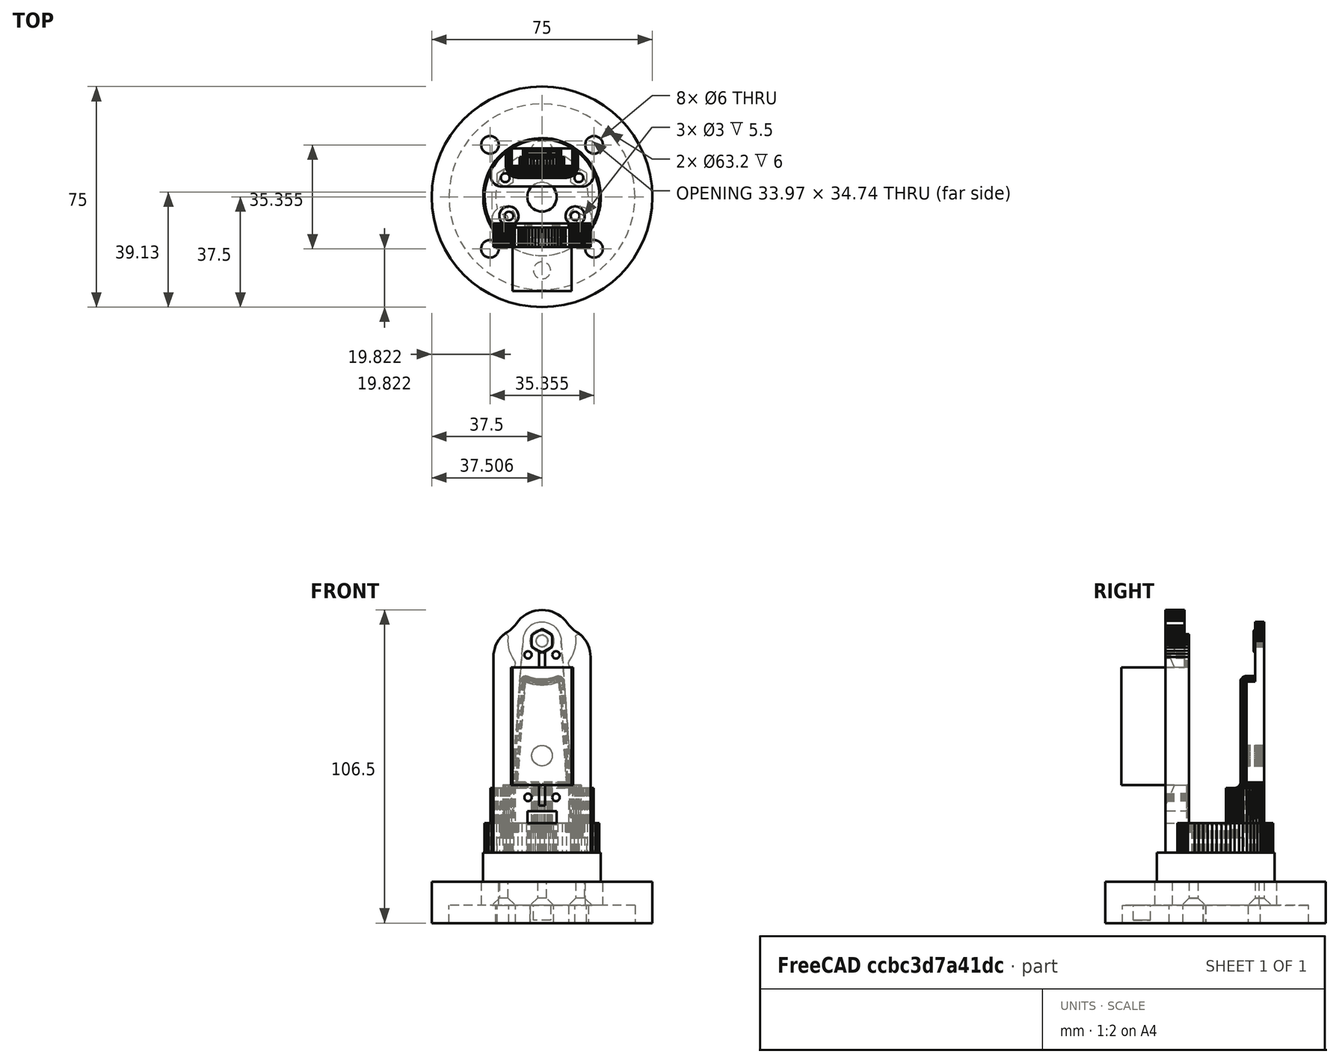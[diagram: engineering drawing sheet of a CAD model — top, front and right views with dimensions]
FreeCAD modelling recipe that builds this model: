
FCSTD DOCUMENT  (FreeCAD 0.16R6703 (Git))
Label: GripperBase
License: All rights reserved
LicenseURL: http://en.wikipedia.org/wiki/All_rights_reserved
objects: Part::Feature×5, Part::MultiFuse×3, Mesh::Feature×2, Sketcher::SketchObject×2, PartDesign::Pad×2
note: 14 computed .brp shape members not serialized (recipe doc carries the construction recipe); baked Part::Feature solids carry a one-line shape summary decoded from their .brp

FEATURE [Mesh::Feature] ServoMount
FEATURE [Mesh::Feature] Mount_B
  Placement = pos=(129.2,99,33.5) rot=(0.707107,-0.707107,0;3.14159rad)
FEATURE [Sketcher::SketchObject] Sketch
  sketch-geometry (4):
    g0: LineSegment StartX=0 StartY=1 StartZ=0 EndX=40 EndY=1 EndZ=0
    g1: LineSegment StartX=40 StartY=1 StartZ=0 EndX=40 EndY=-19 EndZ=0
    g2: LineSegment StartX=40 StartY=-19 StartZ=0 EndX=0 EndY=-19 EndZ=0
    g3: LineSegment StartX=0 StartY=-19 StartZ=0 EndX=0 EndY=1 EndZ=0
  constraints (12):
    c: Coincident(g0,g1)
    c: Coincident(g1,g2)
    c: Coincident(g2,g3)
    c: Horizontal(g0)
    c: Horizontal(g2)
    c: Vertical(g1)
    c: Vertical(g3)
    c: DistanceX(g2,g1) = 40
    c: DistanceY(g1,g0) = 20
    c: Coincident(g3,g0)
    c: PointOnObject(g0,g-2)
    c: DistanceY(g-1,g0) = 1
FEATURE [PartDesign::Pad] Pad
  Length = 15
  Length2 = 100
  Reversed = true
  Sketch = -> Sketch
  Type = 0
FEATURE [Part::Feature] ServoMount001
  shape: bbox 82.5 x 38.99 x 36.48 mm, 2472 faces, 0 solids (baked)
FEATURE [Part::Feature] Mount_B001
  shape: bbox 68.5 x 35.13 x 13 mm, 2276 faces, 0 solids (baked)
FEATURE [Part::Feature] ServoMount001_solid  label="ServoMount001 (Solid)"
  shape: bbox 82.5 x 38.99 x 36.48 mm, 2472 faces (baked)
FEATURE [Part::Feature] Mount_B001_solid  label="Mount_B001 (Solid)"
  shape: bbox 68.5 x 35.13 x 13 mm, 2276 faces (baked)
FEATURE [Part::MultiFuse] Fusion
  Shapes = -> [ServoMount001_solid,Mount_B001_solid]
FEATURE [Part::MultiFuse] Fusion001
  Placement = pos=(10,0,0) rot=(0,0,1;0rad)
  Shapes = -> [Pad,Fusion]
FEATURE [Part::Feature] Pocket001
  Placement = pos=(-31,-9,17) rot=(0.57735,0.57735,0.57735;2.0944rad)
  shape: bbox 14 x 75 x 75 mm, 31 faces (baked)
FEATURE [Part::MultiFuse] Fusion002
  Placement = pos=(9,-17,37) rot=(-0.57735,-0.57735,-0.57735;2.0944rad)
  Shapes = -> [Pocket001,Fusion001]
FEATURE [Sketcher::SketchObject] Sketch001
  Placement = pos=(9,-17,14) rot=(0,0,1;0rad)
  Support = -> Fusion002 [Face33]
  sketch-geometry (1):
    g0: Circle CenterX=-9 CenterY=17 CenterZ=0 NormalX=0 NormalY=0 NormalZ=1 Radius=20
  constraints (3):
    c: Radius(g0) = 20
    c: DistanceY(g-1,g0) = 17
    c: DistanceX(g0,g-1) = 9
FEATURE [PartDesign::Pad] Pad001
  Length = 10
  Length2 = 100
  Placement = pos=(9,-17,37) rot=(-0.57735,-0.57735,-0.57735;2.0944rad)
  Sketch = -> Sketch001
  Type = 0
